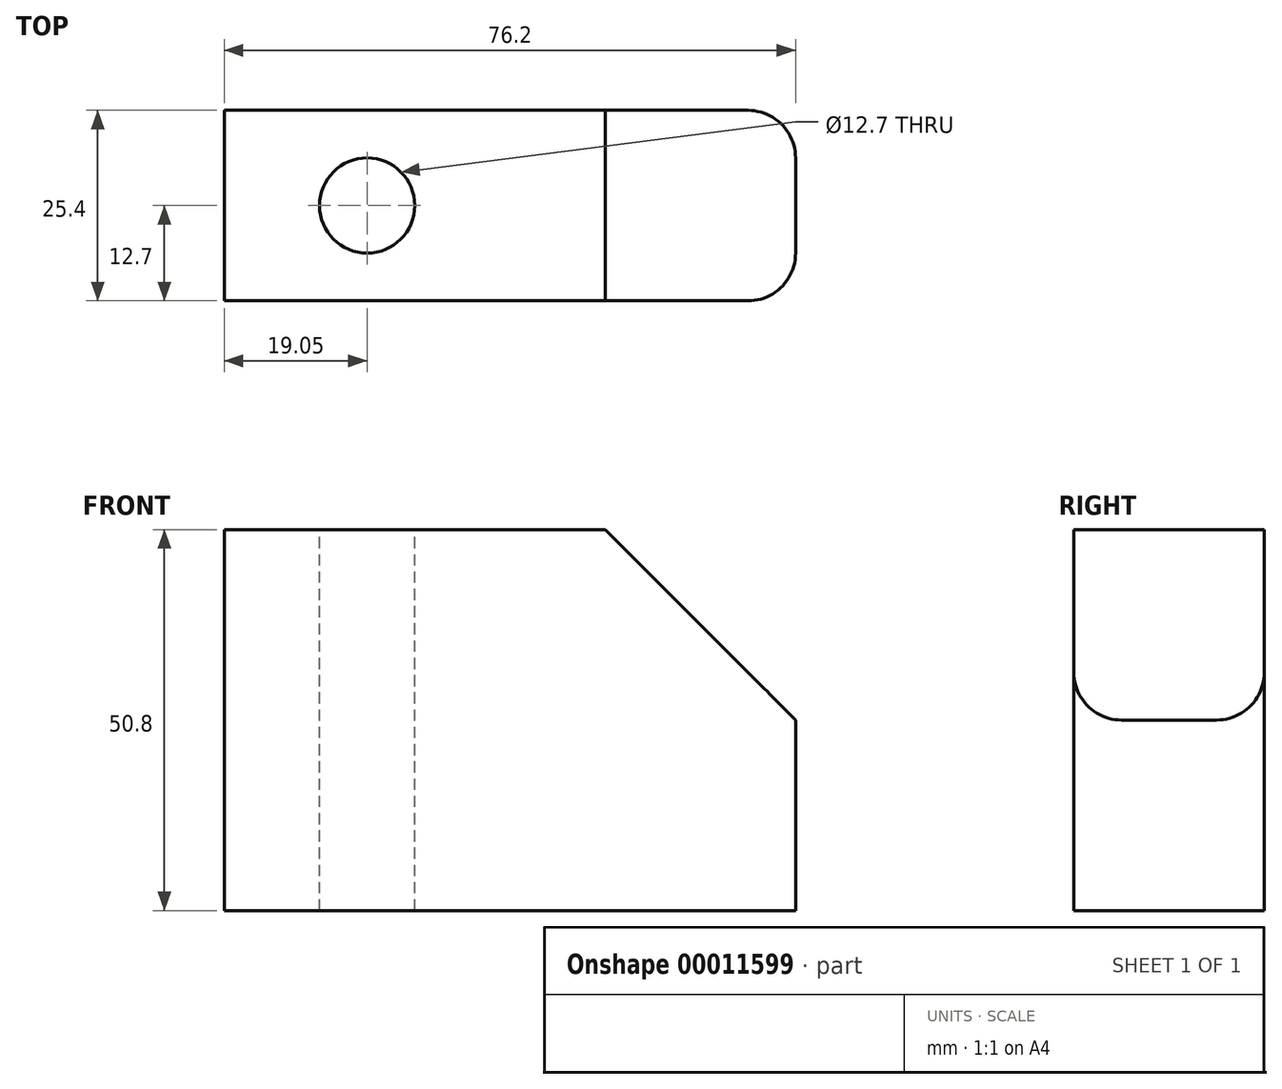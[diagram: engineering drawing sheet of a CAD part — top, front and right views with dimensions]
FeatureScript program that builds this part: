
annotation { "Feature Type Name" : "Feature", "Feature Type Description" : "" }
export const myFeature = defineFeature(function(context is Context, id is Id, definition is map)
    precondition{}
    {
        {
            var Q0;
            Q0=qCreatedBy(makeId("Front.planeOp"),FACE);
            var sketch = newSketch(context, id + "F0", { "sketchPlane" : qUnion([Q0])});
            skLineSegment(sketch, "E0", {"start": v(0, 0) * mm, "end": v(-76.2, 0) * mm});
            skLineSegment(sketch, "E1", {"start": v(-76.2, 0) * mm, "end": v(-76.2, 50.8) * mm});
            skLineSegment(sketch, "E2", {"start": v(-76.2, 50.8) * mm, "end": v(0, 50.8) * mm});
            skLineSegment(sketch, "E3", {"start": v(0, 50.8) * mm, "end": v(0, 0) * mm});
            skSolve(sketch);
        }
        {
            var Q0;
            Q0 = qSketchRegion(id + "F0", true);
            extrude(context, id + "F1", {"entities" : qUnion([Q0]), "oppositeDirection" : true, "depth" : 25.4 * mm});
        }
        {
            var Q0;
            Q0=makeQuery(id+"F1.opExtrude","SWEPT_FACE",FACE,{"disambiguationData":[OSD([sQuery(id+"F0.wireOp",EDGE,"E2")])]});
            var sketch = newSketch(context, id + "F2", { "sketchPlane" : qUnion([Q0])});
            skCircle(sketch, "E4", {"center": v(-57.15, 12.7) * mm, "radius": 6.35 * mm});
            skSolve(sketch);
        }
        {
            var Q0;
            Q0 = qSketchRegion(id + "F2", true);
            extrude(context, id + "F3", {"entities" : qUnion([Q0]), "operationType" : NewBodyOperationType.REMOVE, "endBound" : BoundingType.THROUGH_ALL, "oppositeDirection" : true, "depth" : 25.4 * mm});
        }
        {
            var Q0;
            Q0=makeQuery(id+"F1.opExtrude","SWEPT_EDGE",EDGE,{"disambiguationData":[OSD([sQuery(id+"F0.wireOp",EDGE,"E2"),sQuery(id+"F0.wireOp",EDGE,"E3")])]});
            chamfer(context, id + "F4", {"entities" : qUnion([Q0]), "width" : 25.4 * mm, "tangentPropagation" : true});
        }
        {
            var Q0;
            Q0=makeQuery(id+"F1.opExtrude","CAP_EDGE",EDGE,{"disambiguationData":[OSD([sQuery(id+"F0.wireOp",EDGE,"E3")])],"isStart":true});
            var Q1;
            Q1=makeQuery(id+"F1.opExtrude","CAP_EDGE",EDGE,{"disambiguationData":[OSD([sQuery(id+"F0.wireOp",EDGE,"E3")])],"isStart":false});
            fillet(context, id + "F5", {"entities" : qUnion([Q0, Q1]), "radius" : 6.35 * mm, "tangentPropagation" : true, "allowEdgeOverflow" : false});
        }
    });
